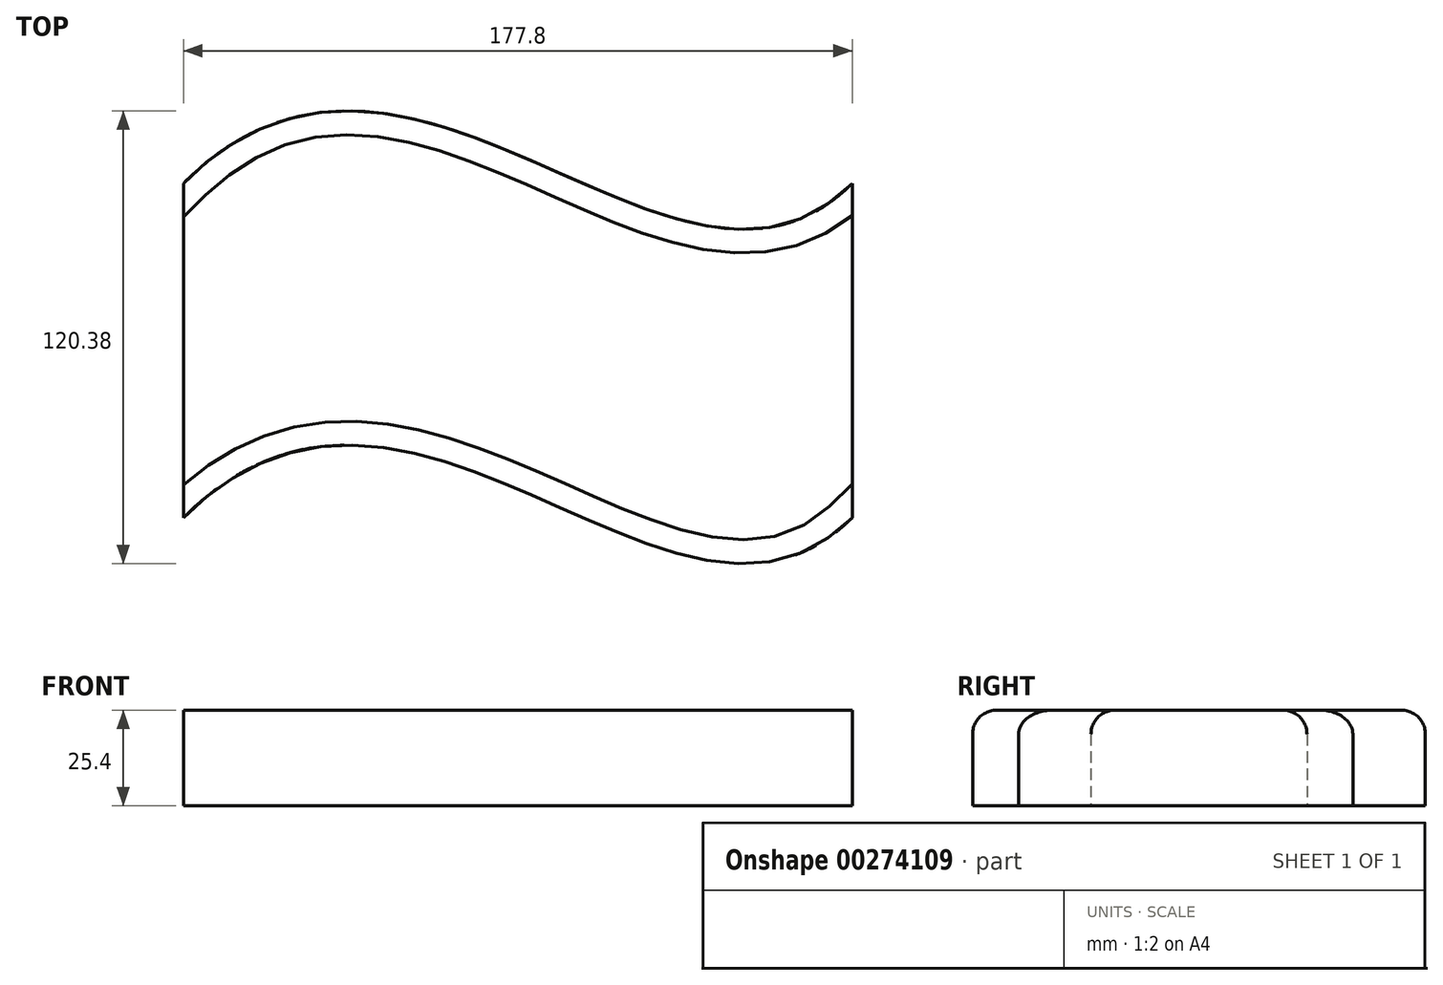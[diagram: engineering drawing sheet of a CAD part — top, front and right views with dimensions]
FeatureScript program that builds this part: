
annotation { "Feature Type Name" : "Feature", "Feature Type Description" : "" }
export const myFeature = defineFeature(function(context is Context, id is Id, definition is map)
    precondition{}
    {
        {
            var Q0;
            Q0=qCreatedBy(makeId("Top.planeOp"),FACE);
            var sketch = newSketch(context, id + "F0", { "sketchPlane" : qUnion([Q0])});
            skLineSegment(sketch, "E0", {"start": v(-61.12, -41.9) * mm, "end": v(-61.12, 47) * mm});
            skLineSegment(sketch, "E1", {"start": v(116.68, -41.9) * mm, "end": v(116.68, 47) * mm});
            skFitSpline(sketch, "E2", {"points": [v(-61.12, 47) * mm, v(116.68, 47) * mm], "startDerivative": vector(183.36, 183.36) * mm, "endDerivative": vector(141, 141) * mm});
            skFitSpline(sketch, "E3", {"points": [v(116.68, -41.9) * mm, v(-61.12, -41.9) * mm], "startDerivative": vector(-141, -141) * mm, "endDerivative": vector(-183.36, -183.36) * mm});
            skLineSegment(sketch, "E4", {"start": v(69.68, 0) * mm, "end": v(116.68, 47) * mm});
            skLineSegment(sketch, "E5", {"start": v(69.68, -88.9) * mm, "end": v(116.68, -41.9) * mm});
            skLineSegment(sketch, "E6", {"start": v(0, 19.22) * mm, "end": v(-61.12, -41.9) * mm});
            skLineSegment(sketch, "E7", {"start": v(0, 108.12) * mm, "end": v(-61.12, 47) * mm});
            skSolve(sketch);
        }
        {
            var Q0;
            Q0 = qSketchRegion(id + "F0", true);
            extrude(context, id + "F1", {"entities" : qUnion([Q0]), "depth" : 25.4 * mm});
        }
        {
            var Q0;
            Q0=makeQuery(id+"F1.opExtrude","CAP_EDGE",EDGE,{"disambiguationData":[OSD([sQuery(id+"F0.wireOp",EDGE,"E2")])],"isStart":false});
            var Q1;
            Q1=makeQuery(id+"F1.opExtrude","CAP_EDGE",EDGE,{"disambiguationData":[OSD([sQuery(id+"F0.wireOp",EDGE,"E3")])],"isStart":false});
            fillet(context, id + "F2", {"entities" : qUnion([Q0, Q1]), "radius" : 6.35 * mm, "tangentPropagation" : true, "allowEdgeOverflow" : false});
        }
    });
